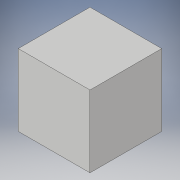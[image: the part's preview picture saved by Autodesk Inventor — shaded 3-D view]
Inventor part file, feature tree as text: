
AUTODESK INVENTOR PART (.ipt)
format: ipt  version: 2017 (Build 210142000, 142)  size: 83,456 bytes
history: native  units: in
note: dims shown in document units (in); Inventor stores cm internally (conversion verified against a paired STEP export)
features: extrude x1, sketch x1
ambient origin geometry x8: Origin, YZ Plane, XZ Plane, XY Plane, X Axis, Y Axis, Z Axis, Center Point
bodies: Solid1 (feature_tree)
feature tree (2):
  extrude  "Extrusion1"  Depth=50.0in
  sketch  "Sketch1"  dims[d0=50.0in d1=50.0in d2=50.0in d3=0.0in]
